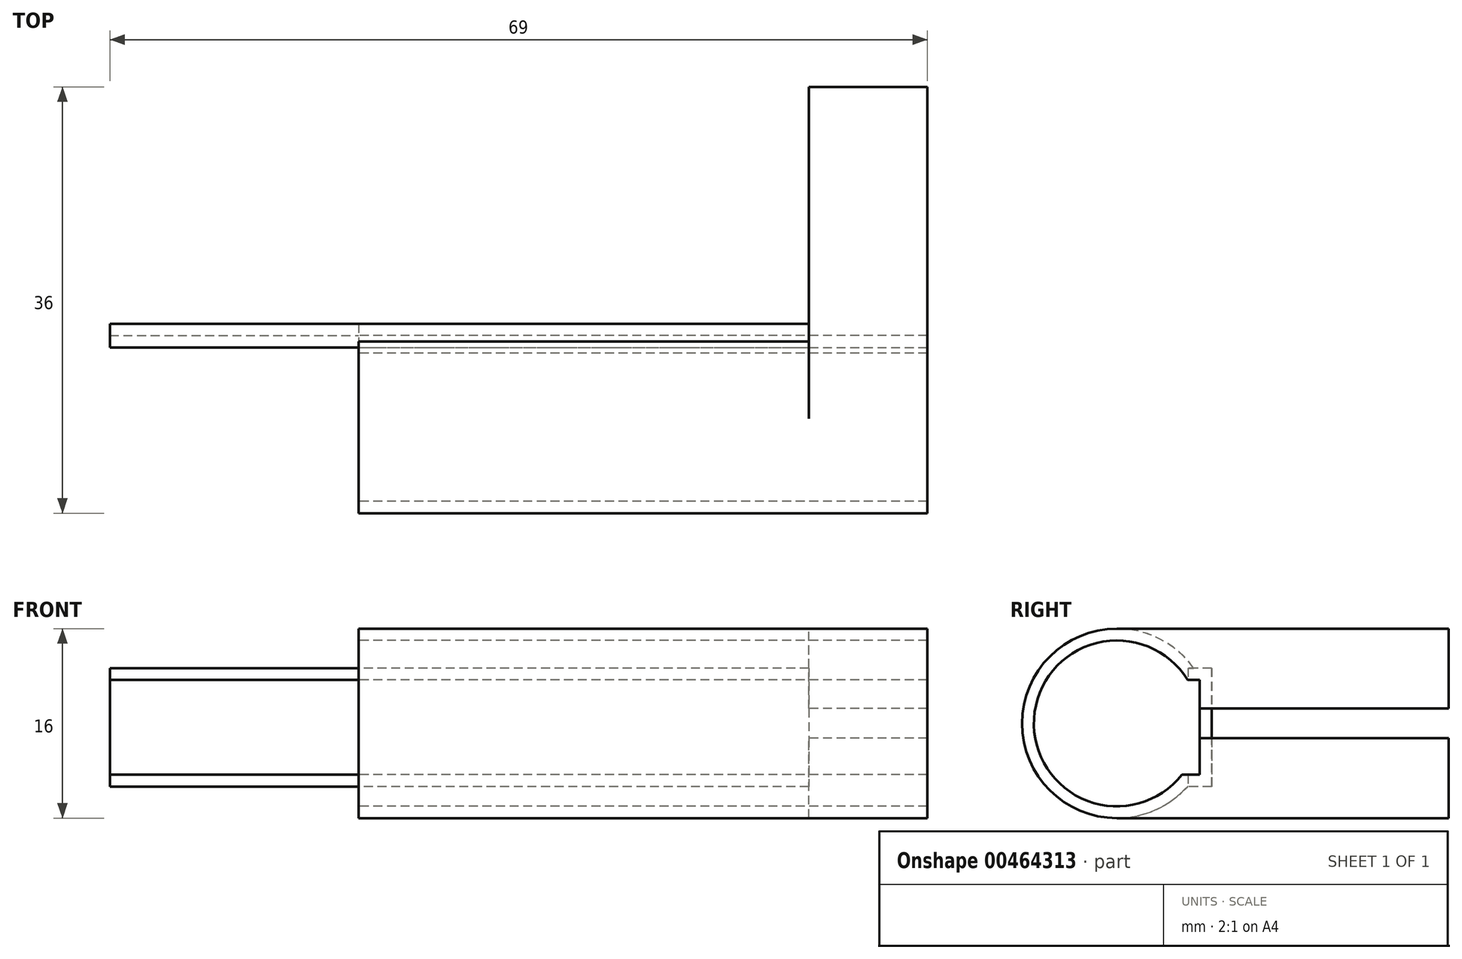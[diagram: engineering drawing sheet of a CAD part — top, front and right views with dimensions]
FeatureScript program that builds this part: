
annotation { "Feature Type Name" : "Feature", "Feature Type Description" : "" }
export const myFeature = defineFeature(function(context is Context, id is Id, definition is map)
    precondition{}
    {
        {
            var Q0;
            Q0=qCreatedBy(makeId("Right.planeOp"),FACE);
            var sketch = newSketch(context, id + "F0", { "sketchPlane" : qUnion([Q0])});
            skArc(sketch, "E0", {"start": v(5.96, 10.34) * mm, "mid": v(-6.99, 7.08) * mm, "end": v(5.5, 2.34) * mm});
            skLineSegment(sketch, "E1.bottom", {"start": v(7, 10.34) * mm, "end": v(5.5, 10.34) * mm});
            skLineSegment(sketch, "E1.top", {"start": v(7, 2.34) * mm, "end": v(5.87, 2.34) * mm});
            skLineSegment(sketch, "E1.left", {"start": v(7, 10.34) * mm, "end": v(7, 2.34) * mm});
            skLineSegment(sketch, "E2", {"start": v(5.96, 10.34) * mm, "end": v(5.5, 10.34) * mm});
            skLineSegment(sketch, "E3", {"start": v(5.87, 2.34) * mm, "end": v(5.5, 2.34) * mm});
            skLineSegment(sketch, "E4.0", {"start": v(8, 11.34) * mm, "end": v(8, 1.34) * mm});
            skLineSegment(sketch, "E4.1", {"start": v(8, 11.34) * mm, "end": v(6.5, 11.34) * mm});
            skArc(sketch, "E4.2", {"start": v(6.5, 11.34) * mm, "mid": v(-7.99, 7.1) * mm, "end": v(5.96, 1.34) * mm});
            skLineSegment(sketch, "E4.3", {"start": v(8, 1.34) * mm, "end": v(5.96, 1.34) * mm});
            skSolve(sketch);
        }
        {
            var Q0;
            Q0=makeQuery(id+"F0.imprint","IMPRINT",FACE,{"disambiguationData":[TD([[makeQuery(id+"F0.imprint","IMPRINT",EDGE,{"derivedFrom":sQuery(id+"F0.wireOp",EDGE,"E0")}),-1.0]])]});
            var Q1;
            Q1 = qConstructionFilter(qBodyType(qCreatedBy(id + "F0" ,EDGE), BodyType.WIRE), ConstructionObject.NO);
            extrude(context, id + "F1", {"entities" : qUnion([Q0]), "surfaceEntities" : qUnion([Q1]), "depth" : 38 * mm});
        }
        {
            var Q0;
            Q0=qCreatedBy(makeId("Right.planeOp"),FACE);
            var sketch = newSketch(context, id + "F2", { "sketchPlane" : qUnion([Q0])});
            skLineSegment(sketch, "E5.bottom", {"start": v(7.98, 11.34) * mm, "end": v(6, 11.34) * mm});
            skLineSegment(sketch, "E5.top", {"start": v(7.98, 1.32) * mm, "end": v(6, 1.32) * mm});
            skLineSegment(sketch, "E5.left", {"start": v(7.98, 11.34) * mm, "end": v(7.98, 1.32) * mm});
            skLineSegment(sketch, "E5.right", {"start": v(6, 11.34) * mm, "end": v(6, 10.34) * mm});
            skLineSegment(sketch, "E6.bottom", {"start": v(7, 10.34) * mm, "end": v(6, 10.34) * mm});
            skLineSegment(sketch, "E6.top", {"start": v(7, 2.34) * mm, "end": v(6, 2.34) * mm});
            skLineSegment(sketch, "E6.left", {"start": v(7, 10.34) * mm, "end": v(7, 2.34) * mm});
            skLineSegment(sketch, "E7.trimOffspring", {"start": v(6, 2.34) * mm, "end": v(6, 1.32) * mm});
            skSolve(sketch);
        }
        {
            var Q0;
            Q0 = qSketchRegion(id + "F2", true);
            extrude(context, id + "F3", {"entities" : qUnion([Q0]), "operationType" : NewBodyOperationType.ADD, "oppositeDirection" : true, "depth" : 21 * mm});
        }
        {
            var Q0;
            Q0=makeQuery(id+"F1.opExtrude","CAP_FACE",FACE,{"disambiguationData":[OSD([sQuery(id+"F0.wireOp",EDGE,"E0"),sQuery(id+"F0.wireOp",EDGE,"E1.bottom"),sQuery(id+"F0.wireOp",EDGE,"E1.top"),sQuery(id+"F0.wireOp",EDGE,"E1.left"),sQuery(id+"F0.wireOp",EDGE,"E2"),sQuery(id+"F0.wireOp",EDGE,"E3"),sQuery(id+"F0.wireOp",EDGE,"E4.0"),sQuery(id+"F0.wireOp",EDGE,"E4.1"),sQuery(id+"F0.wireOp",EDGE,"E4.2"),sQuery(id+"F0.wireOp",EDGE,"E4.3")])],"isStart":false});
            var sketch = newSketch(context, id + "F4", { "sketchPlane" : qUnion([Q0])});
            skLineSegment(sketch, "E8.bottom", {"start": v(0, -1.32) * mm, "end": v(28, -1.32) * mm});
            skLineSegment(sketch, "E8.top", {"start": v(0, 14.68) * mm, "end": v(28, 14.68) * mm});
            skLineSegment(sketch, "E8.right", {"start": v(28, -1.32) * mm, "end": v(28, 5.43) * mm});
            skLineSegment(sketch, "E9.top", {"start": v(8, 5.43) * mm, "end": v(12.79, 5.43) * mm});
            skPoint(sketch, "E10", {"position": v(13.29, 7.93) * mm});
            skLineSegment(sketch, "E11", {"start": v(13.29, 7.93) * mm, "end": v(28, 7.93) * mm});
            skLineSegment(sketch, "E12", {"start": v(12.79, 5.43) * mm, "end": v(28, 5.43) * mm});
            skArc(sketch, "E13.trimOffspring", {"start": v(0, 14.68) * mm, "mid": v(-8, 6.68) * mm, "end": v(0, -1.32) * mm});
            skLineSegment(sketch, "E14.trimOffspring", {"start": v(28, 7.93) * mm, "end": v(28, 14.68) * mm});
            skPoint(sketch, "E15.end.orphan", {"position": v(8, 5.43) * mm});
            skLineSegment(sketch, "E16", {"start": v(13.29, 7.93) * mm, "end": v(8, 7.93) * mm});
            skLineSegment(sketch, "E17", {"start": v(8, 7.93) * mm, "end": v(7, 7.93) * mm});
            skPoint(sketch, "E17.endSnap0", {"position": v(7, 6.34) * mm});
            skLineSegment(sketch, "E18", {"start": v(8, 5.43) * mm, "end": v(7, 5.43) * mm});
            skPoint(sketch, "E19", {"position": v(5.96, 10.34) * mm});
            skPoint(sketch, "E20", {"position": v(5.5, 2.34) * mm});
            skLineSegment(sketch, "E21", {"start": v(5.96, 10.34) * mm, "end": v(7, 10.34) * mm});
            skLineSegment(sketch, "E22", {"start": v(7, 10.34) * mm, "end": v(7, 7.93) * mm});
            skLineSegment(sketch, "E23", {"start": v(5.5, 2.34) * mm, "end": v(7, 2.34) * mm});
            skLineSegment(sketch, "E24", {"start": v(7, 2.34) * mm, "end": v(7, 5.43) * mm});
            skArc(sketch, "E25", {"start": v(5.96, 10.34) * mm, "mid": v(-6.99, 7.08) * mm, "end": v(5.5, 2.34) * mm});
            skSolve(sketch);
        }
        {
            var Q0;
            Q0 = qSketchRegion(id + "F4", true);
            extrude(context, id + "F5", {"entities" : qUnion([Q0]), "operationType" : NewBodyOperationType.ADD, "depth" : 10 * mm});
        }
    });
